# Revit family: РВК_Угольник комбинированный ВР
name_source: partatom
category: Соединительные детали трубопроводов
revit_build: Autodesk Revit 2016 (Build: 20150714_1515(x64)
units: mm (PartAtom-declared; Revit-internal decimal feet)

## family parameters
Всегда вертикально = Да
На основе рабочей плоскости = Нет
Общий = Нет
При загрузке вырезать с полостями = Нет
Размер круглого соединителя = Использовать радиус
Тип детали = Отвод

## types (4) — shared parameters
1 = 1 мм
ADSK_Завод-изготовитель = РВК
F = 20 мм
Материал фитинга = РВК_Полипропилен PPR

## per-type parameters (varying)
| type | A | B | C | D | E | G | I | L1 | L1-A | L2 | M | N | Q | R | g | r |
| Угольник комбинированный ПП D25-3/4'' BP | 17 мм | 42 мм | 22 мм | 25 мм | 41 мм | 25 мм | 18 мм | 31 мм | 14 мм | 33 мм | 28 мм | 17 мм | 12 мм | 17 мм | 13 мм | 13 мм |
| Угольник комбинированный ПП D25-1/2'' BP | 17 мм | 34 мм | 22 мм | 25 мм | 35 мм | 20 мм | 14 мм | 30 мм | 13 мм | 30 мм | 26 мм | 15 мм | 11 мм | 17 мм | 13 мм | 10 мм |
| Угольник комбинированный ПП D20-3/4'' BP | 15 мм | 29 мм | 15 мм | 20 мм | 40 мм | 25 мм | 18 мм | 30 мм | 15 мм | 30 мм | 32 мм | 17 мм | 12 мм | 15 мм | 10 мм | 13 мм |
| Угольник комбинированный ПП D20-1/2'' BP | 15 мм | 29 мм | 15 мм | 20 мм | 35 мм | 20 мм | 14 мм | 26 мм | 11 мм | 28 мм | 26 мм | 15 мм | 11 мм | 15 мм | 10 мм | 10 мм |

note: column(s) folded — value = type name in every type: Type

## geometry (parser evidence)
native form markers: Blend x4
no freeform markers — native parametric forms only
